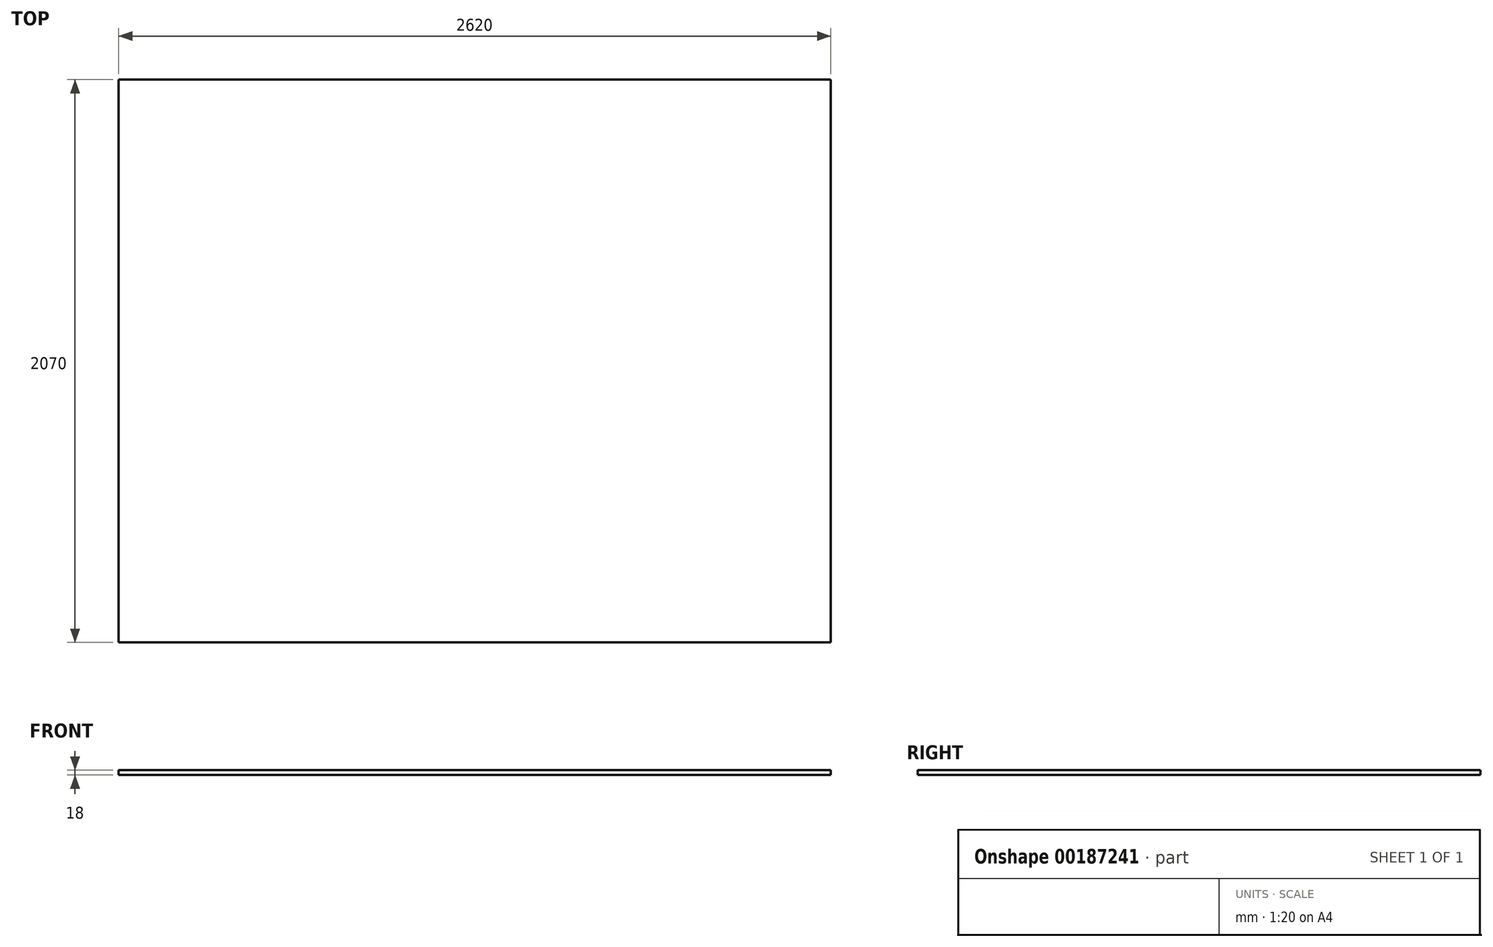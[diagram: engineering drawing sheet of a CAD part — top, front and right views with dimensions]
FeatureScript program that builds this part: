
annotation { "Feature Type Name" : "Feature", "Feature Type Description" : "" }
export const myFeature = defineFeature(function(context is Context, id is Id, definition is map)
    precondition{}
    {
        {
            var Q0;
            Q0=qCreatedBy(makeId("Top.planeOp"),FACE);
            var sketch = newSketch(context, id + "F0", { "sketchPlane" : qUnion([Q0])});
            skLineSegment(sketch, "E0.bottom", {"start": v(1310, 1035) * mm, "end": v(-1310, 1035) * mm});
            skLineSegment(sketch, "E0.top", {"start": v(1310, -1035) * mm, "end": v(-1310, -1035) * mm});
            skLineSegment(sketch, "E0.left", {"start": v(1310, 1035) * mm, "end": v(1310, -1035) * mm});
            skLineSegment(sketch, "E0.right", {"start": v(-1310, 1035) * mm, "end": v(-1310, -1035) * mm});
            skPoint(sketch, "E0.middle", {"position": v(0, 0) * mm});
            skSolve(sketch);
        }
        {
            var Q0;
            Q0=makeQuery(id+"F0.imprint","IMPRINT",FACE,{"disambiguationData":[TD([[makeQuery(id+"F0.imprint","IMPRINT",EDGE,{"derivedFrom":sQuery(id+"F0.wireOp",EDGE,"E0.bottom")}),1.0]])]});
            extrude(context, id + "F1", {"entities" : qUnion([Q0]), "depth" : 18 * mm});
        }
    });
